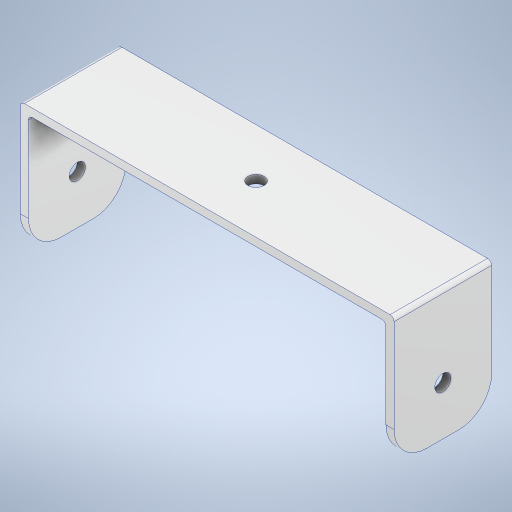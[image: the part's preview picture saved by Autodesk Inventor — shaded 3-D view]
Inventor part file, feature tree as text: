
AUTODESK INVENTOR PART (.ipt)
format: ipt  version: 2024 (Build 280153000, 153)  size: 264,192 bytes
history: native  units: in
note: dims shown in document units (in); Inventor stores cm internally (conversion verified against a paired STEP export)
features: extrude x3, sketch x3, fillet x2
ambient origin geometry x8: Origin, YZ Plane, XZ Plane, XY Plane, X Axis, Y Axis, Z Axis, Center Point
bodies: Body1 (feature_tree)
feature tree (8):
  extrude  "Extrusion4"  Depth=3.0in
  extrude  "Extrusion5"  Depth=4.0in
  fillet  "Fillet4"  Radius=4.0in
  extrude  "Extrusion6"  Depth=0.25in
  fillet  "Fillet5"  Radius=0.25in
  sketch  "Sketch1"  dims[d0=11.5in d1=3.0in]
  sketch  "Sketch4"  dims[d27=0.5in d28=1.5in d30=4.0in d31=0.0in]
  sketch  "Sketch5"  dims[d32=0.25in d33=0.25in d34=0.25in d35=4.6875in d36=0.0in d37=1.0in d38=0.5in d39=2.5in d40=1.5in d41=13.0in d42=0.0in d43=5.75in d44=0.125in d45=5.75in d46=5.75in]
